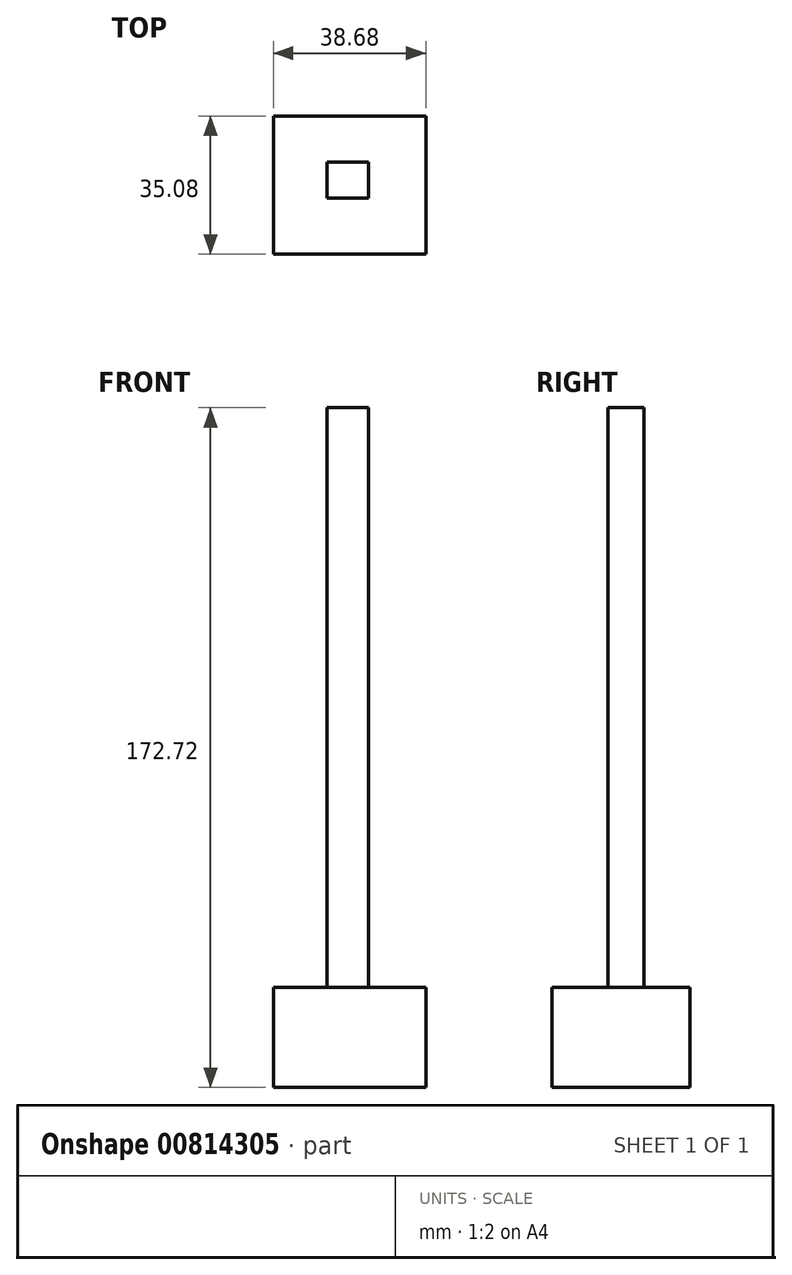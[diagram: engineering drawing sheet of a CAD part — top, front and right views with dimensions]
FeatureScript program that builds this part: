
annotation { "Feature Type Name" : "Feature", "Feature Type Description" : "" }
export const myFeature = defineFeature(function(context is Context, id is Id, definition is map)
    precondition{}
    {
        {
            var Q0;
            Q0=qCreatedBy(makeId("Top.planeOp"),FACE);
            var sketch = newSketch(context, id + "F0", { "sketchPlane" : qUnion([Q0])});
            skLineSegment(sketch, "E0.bottom", {"start": v(-38.68, 35.08) * mm, "end": v(0, 35.08) * mm});
            skLineSegment(sketch, "E0.top", {"start": v(-38.68, 0) * mm, "end": v(0, 0) * mm});
            skLineSegment(sketch, "E0.left", {"start": v(-38.68, 35.08) * mm, "end": v(-38.68, 0) * mm});
            skLineSegment(sketch, "E0.right", {"start": v(0, 35.08) * mm, "end": v(0, 0) * mm});
            skSolve(sketch);
        }
        {
            var Q0;
            Q0 = qSketchRegion(id + "F0", true);
            extrude(context, id + "F1", {"entities" : qUnion([Q0]), "depth" : 25.4 * mm, "offsetDistance" : 25.4 * mm});
        }
        {
            var Q0;
            Q0=makeQuery(id+"F1.opExtrude","CAP_FACE",FACE,{"disambiguationData":[OSD([sQuery(id+"F0.wireOp",EDGE,"E0.bottom"),sQuery(id+"F0.wireOp",EDGE,"E0.top"),sQuery(id+"F0.wireOp",EDGE,"E0.left"),sQuery(id+"F0.wireOp",EDGE,"E0.right")])],"isStart":false});
            var sketch = newSketch(context, id + "F2", { "sketchPlane" : qUnion([Q0])});
            skLineSegment(sketch, "E1.bottom", {"start": v(-25.12, 23.4) * mm, "end": v(-14.56, 23.4) * mm});
            skLineSegment(sketch, "E1.top", {"start": v(-25.12, 14.28) * mm, "end": v(-14.56, 14.28) * mm});
            skLineSegment(sketch, "E1.left", {"start": v(-25.12, 23.4) * mm, "end": v(-25.12, 14.28) * mm});
            skLineSegment(sketch, "E1.right", {"start": v(-14.56, 23.4) * mm, "end": v(-14.56, 14.28) * mm});
            skPoint(sketch, "E1.middle", {"position": v(-19.84, 18.84) * mm});
            skSolve(sketch);
        }
        {
            var Q0;
            Q0 = qSketchRegion(id + "F2", true);
            extrude(context, id + "F3", {"entities" : qUnion([Q0]), "operationType" : NewBodyOperationType.ADD, "depth" : 147.32 * mm, "offsetDistance" : 25.4 * mm});
        }
    });
